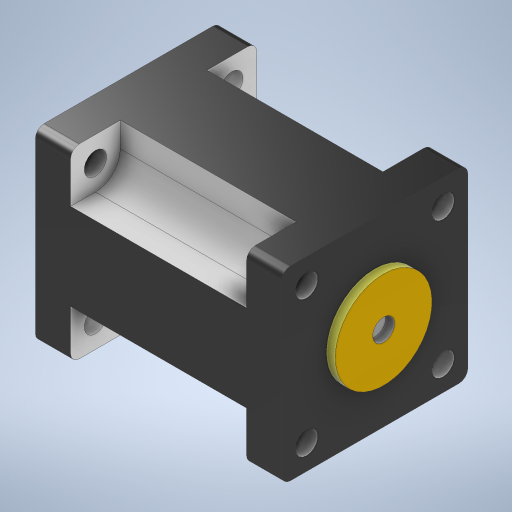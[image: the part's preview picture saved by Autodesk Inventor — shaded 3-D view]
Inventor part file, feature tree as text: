
AUTODESK INVENTOR PART (.ipt)
format: ipt  version: 2023.2 (Build 272271030, 271C)  size: 328,192 bytes
history: native  units: mm
features: extrude x4, sketch x3, plane x1, fillet x1, pattern_circular x1, projected_geometry x1
ambient origin geometry x8: Origin, YZ Plane, XZ Plane, XY Plane, X Axis, Y Axis, Z Axis, Center Point
bodies: Solid1 (feature_tree)
feature tree (11):
  extrude  "Extrusion1"  Depth=42.3mm
  plane  "Work Plane1"
  sketch  "Sketch2"  dims[d2=56.0mm d3=0.0mm d4=28.0mm d5=22.0mm]
  extrude  "Extrusion2"  Depth=28.0mm
  fillet  "Fillet1"  Radius=22.0mm
  pattern_circular  "Circular Pattern1"  [2 undecoded]
  extrude  "Extrusion4"  Depth=2.0mm
  extrude  "Extrusion6"  Depth=40.0mm TaperAngle=360.0deg
  sketch  "Sketch1"  dims[d0=42.3mm d1=42.3mm]
  sketch  "Sketch3"  dims[d6=5.0mm d7=2.0mm d8=0.0mm d11=2.0mm d12=40.0mm d13=360.0deg d15=5.1mm d16=31.0mm d17=31.0mm d18=0.0mm d19=0.0mm d20=1.0mm d23=40.0mm d24=0.0mm d25=11.3mm]
  projected_geometry  "Projected Loop1"
note: 2 required parameter values undecoded (feature->parameter linkage not recoverable at this tier; creation-order binding heuristic only, values carry confidence <= 0.55)
